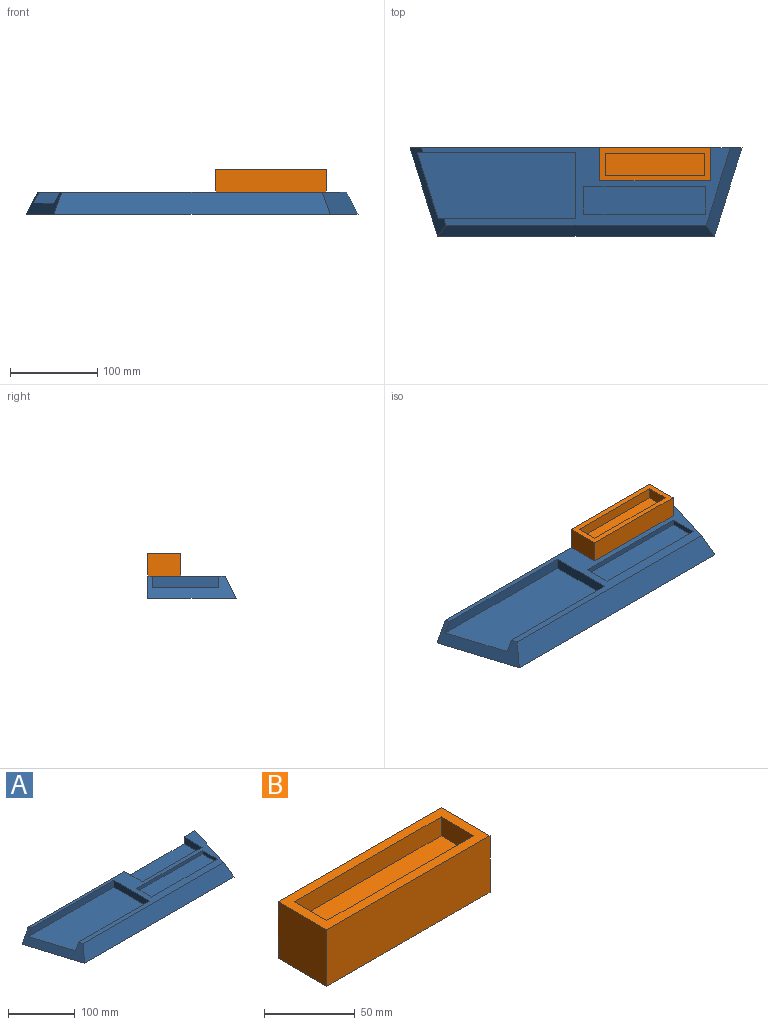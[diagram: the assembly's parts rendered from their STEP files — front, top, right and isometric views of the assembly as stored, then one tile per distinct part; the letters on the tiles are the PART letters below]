
ASSEMBLY  parts=2 mates=1
PART A: 19 faces, bbox 381x101.6x25.4 mm
  f0: plane 381x25.4mm, normal (0,1,0), area 7726.5mm2, adj f1,f2,f3,f5,f15,f17,f18
  f1: plane 354.39x88.9mm, normal (0,0,1), area 7325.4mm2, adj f0,f2,f4,f5,f6,f7,f8,f9
  f2: plane 101.6x41.09mm, normal (-0.85,-0.27,0.45), area 1700.3mm2, adj f0,f1,f3,f4,f11,f13,f14
  f3: plane 381x101.6mm, normal (0,0,-1), area 35483.8mm2, adj f0,f2,f4,f5
  f4: plane 317.5x25.4mm, normal (0,-0.89,0.45), area 8751.2mm2, adj f1,f2,f3,f5
  f5: plane 101.6x41.09mm, normal (0.85,-0.27,0.45), area 2833.9mm2, adj f0,f1,f3,f4
  f6: plane 139.7x6.35mm, normal (0,-1,0), area 887.1mm2, adj f1,f7,f9,f10
  f7: plane 31.75x6.35mm, normal (1,0,0), area 201.6mm2, adj f1,f6,f8,f10
  f8: plane 139.7x6.35mm, normal (0,1,0), area 887.1mm2, adj f1,f7,f9,f10
  f9: plane 31.75x6.35mm, normal (-1,0,0), area 201.6mm2, adj f1,f6,f8,f10
  f10: plane 139.7x31.75mm, normal (0,0,1), area 4435.5mm2, adj f6,f7,f8,f9
  f11: plane 157.95x12.7mm, normal (0,1,0), area 1963.7mm2, adj f1,f2,f12,f14
  f12: plane 76.2x12.7mm, normal (-1,0,0), area 967.7mm2, adj f1,f11,f13,f14
  f13: plane 181.76x12.7mm, normal (0,-1,0), area 2266.1mm2, adj f1,f2,f12,f14
  f14: plane 181.76x76.2mm, normal (0,0,1), area 12942.8mm2, adj f2,f11,f12,f13
  f15: plane 38.1x12.7mm, normal (1,0,0), area 483.9mm2, adj f0,f1,f16,f18
  f16: plane 127x12.7mm, normal (0,1,0), area 1612.9mm2, adj f1,f15,f17,f18
  f17: plane 38.1x12.7mm, normal (-1,0,0), area 483.9mm2, adj f0,f1,f16,f18
  f18: plane 127x38.1mm, normal (0,0,1), area 4838.7mm2, adj f0,f15,f16,f17
PART B: 11 faces, bbox 127x38.1x38.1 mm
  f0: plane 127x38.1mm, normal (0,1,0), area 4838.7mm2, adj f1,f3,f4,f5
  f1: plane 38.1x38.1mm, normal (-1,0,0), area 1451.6mm2, adj f0,f2,f4,f5
  f2: plane 127x38.1mm, normal (0,-1,0), area 4838.7mm2, adj f1,f3,f4,f5
  f3: plane 38.1x38.1mm, normal (1,0,0), area 1451.6mm2, adj f0,f2,f4,f5
  f4: plane 127x38.1mm, normal (0,0,1), area 1935.5mm2, adj f0,f1,f2,f3,f6,f7,f8,f9
  f5: plane 127x38.1mm, normal (0,0,-1), area 4838.7mm2, adj f0,f1,f2,f3
  f6: plane 114.3x12.7mm, normal (0,-1,0), area 1451.6mm2, adj f4,f7,f9,f10
  f7: plane 25.4x12.7mm, normal (1,0,0), area 322.6mm2, adj f4,f6,f8,f10
  f8: plane 114.3x12.7mm, normal (0,1,0), area 1451.6mm2, adj f4,f7,f9,f10
  f9: plane 25.4x12.7mm, normal (-1,0,0), area 322.6mm2, adj f4,f6,f8,f10
  f10: plane 114.3x25.4mm, normal (0,0,1), area 2903.2mm2, adj f6,f7,f8,f9
PLACE A t=(-122.74,-65.4,-41.5)mm
PLACE B t=(67.5,93.7,-28.8)mm
MATE fastened B.f5 <-> A.f18  axis (0,0,-1) through (-59.24,-22.05,-28.8)mm
